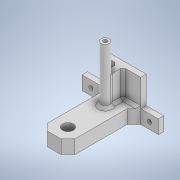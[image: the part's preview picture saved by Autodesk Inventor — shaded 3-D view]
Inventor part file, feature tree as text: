
AUTODESK INVENTOR PART (.ipt)
format: ipt  version: 2022 (Build 260153000, 153)  size: 183,296 bytes
history: native  units: mm
features: sketch x6, extrude x5, chamfer x3, hole x2, other x1
ambient origin geometry x8: Origin, YZ Plane, XZ Plane, XY Plane, X Axis, Y Axis, Z Axis, Center Point
bodies: Body1 (feature_tree)
feature tree (17):
  other  "Sólido1"
  sketch  "Esboço1"  dims[d0=56.0mm d1=10.0mm]
  extrude  "Extrusão1"  Depth=10.0mm
  extrude  "Extrusão2"  Depth=4.0mm TaperAngle=0.0deg
  chamfer  "Chanfro1"  Distance=52.426mm
  hole  "Furo1"  [1 undecoded]
  hole  "Furo2"  [1 undecoded]
  extrude  "Extrusão3"  Depth=3.0mm TaperAngle=0.0deg
  extrude  "Extrusão4"  TaperAngle=0.0deg  [1 undecoded]
  extrude  "Extrusão5"  Depth=3.0mm TaperAngle=0.0deg
  chamfer  "Chanfro2"  Distance=2.0mm Angle=45.0deg
  chamfer  "Chanfro3"  Distance=1.0mm Angle=45.0deg
  sketch  "Esboço2"  dims[d2=20.0mm d3=4.0mm d4=0.0mm d5=52.426mm d6=0.0mm]
  sketch  "Esboço3"  dims[d7=5.0mm d8=2.0mm d9=45.0deg]
  sketch  "Esboço4"  dims[d10=8.0mm d11=6.0mm d12=4.0mm d13=2.0mm d14=90.0deg d15=8.0mm d16=20.594885mm]
  sketch  "Esboço5"  dims[d17=3.0mm d18=6.0mm d19=4.0mm d20=2.0mm d21=90.0deg d22=8.0mm d23=20.594885mm d24=10.0mm]
  sketch  "Esboço6"  dims[d25=3.0mm d26=6.0mm d27=41.0mm d28=0.0mm d29=0.0mm d30=0.0mm d33=20.0mm d34=0.0mm d35=2.0mm d36=2.0mm d37=45.0deg d38=1.0mm d39=2.0mm d40=45.0deg]
note: 3 required parameter values undecoded (feature->parameter linkage not recoverable at this tier; creation-order binding heuristic only, values carry confidence <= 0.55)
